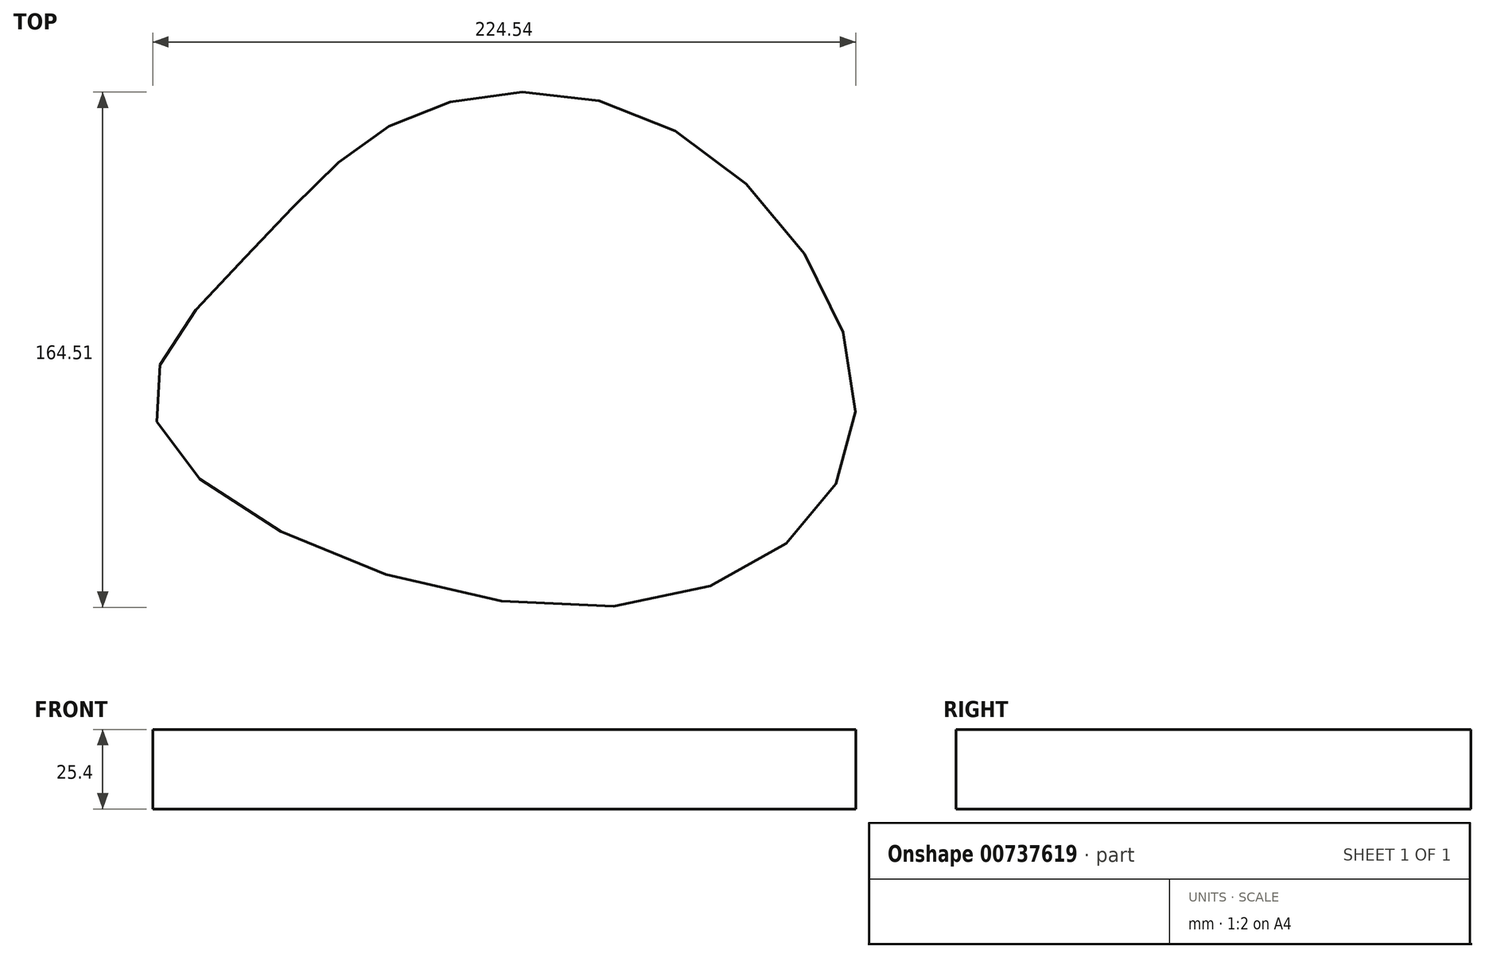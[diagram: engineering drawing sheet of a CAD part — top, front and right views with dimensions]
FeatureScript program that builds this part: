
annotation { "Feature Type Name" : "Feature", "Feature Type Description" : "" }
export const myFeature = defineFeature(function(context is Context, id is Id, definition is map)
    precondition{}
    {
        {
            var Q0;
            Q0=qCreatedBy(makeId("Top.planeOp"),FACE);
            var sketch = newSketch(context, id + "F0", { "sketchPlane" : qUnion([Q0])});
            skFitSpline(sketch, "E0", {"points": [v(-118.49, 0) * mm, v(-88.05, 54.61) * mm, v(-38.12, 97.41) * mm, v(47.03, 92.95) * mm, v(104.55, 0) * mm, v(25.19, -59.07) * mm, v(-118.49, 0) * mm]});
            skSolve(sketch);
        }
        {
            var Q0;
            Q0=makeQuery(id+"F0.imprint","IMPRINT",FACE,{"disambiguationData":[TD([[makeQuery(id+"F0.imprint","IMPRINT",EDGE,{"derivedFrom":sQuery(id+"F0.wireOp",EDGE,"E0")}),-1.0]])]});
            extrude(context, id + "F1", {"entities" : qUnion([Q0]), "depth" : 25.4 * mm, "offsetDistance" : 25.4 * mm});
        }
    });
